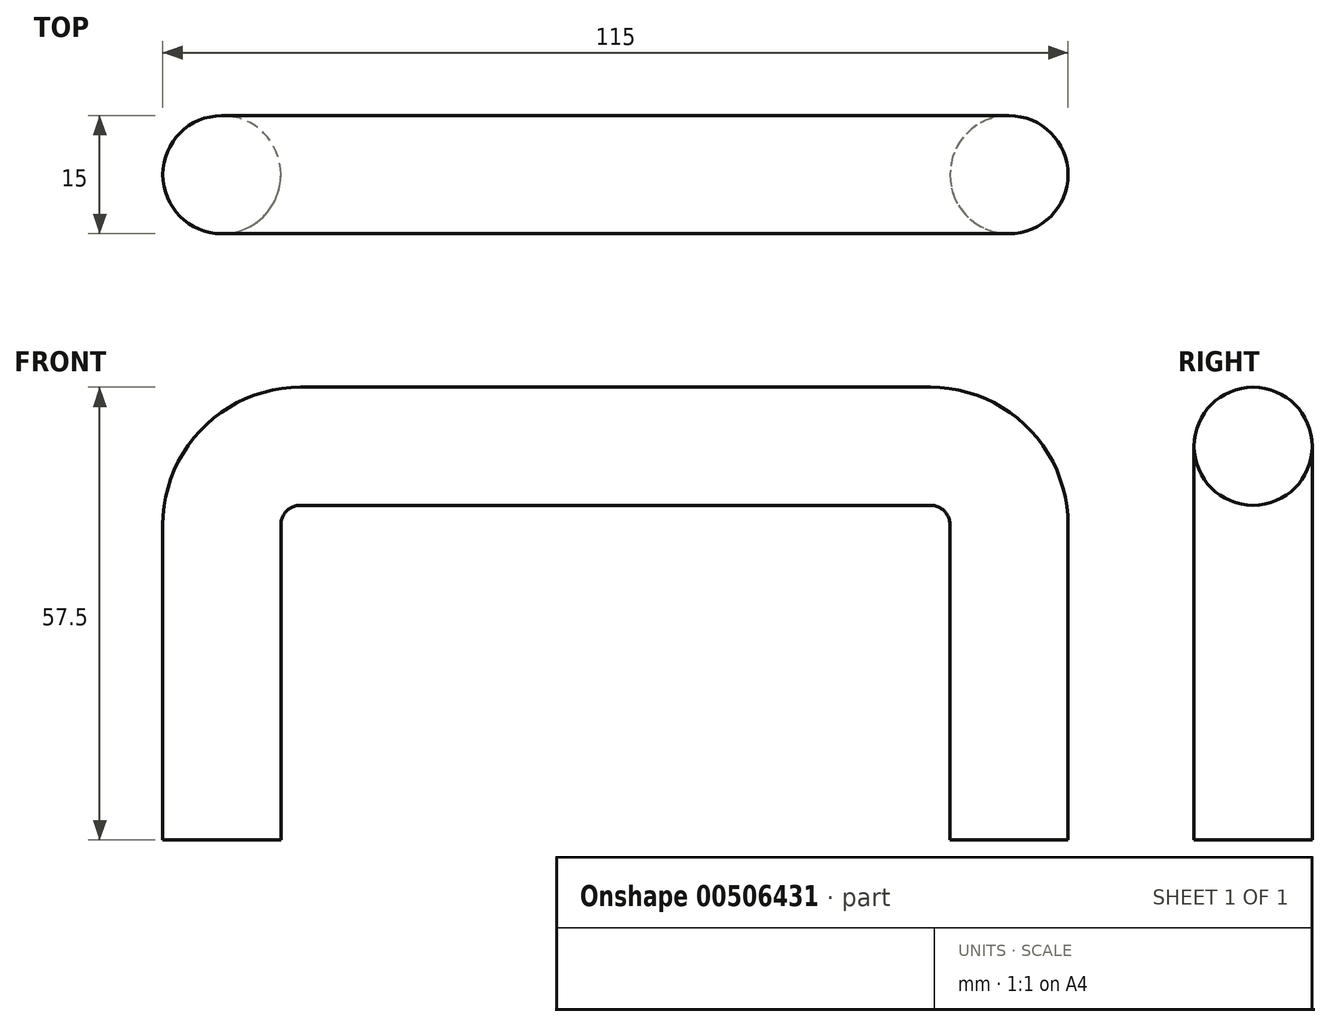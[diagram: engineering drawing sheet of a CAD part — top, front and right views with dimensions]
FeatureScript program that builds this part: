
annotation { "Feature Type Name" : "Feature", "Feature Type Description" : "" }
export const myFeature = defineFeature(function(context is Context, id is Id, definition is map)
    precondition{}
    {
        {
            var Q0;
            Q0=qCreatedBy(makeId("Top.planeOp"),FACE);
            cPlane(context, id + "F0", {"entities" : qUnion([Q0]), "cplaneType" : CPlaneType.OFFSET, "offset" : 25 * mm, "oppositeDirection" : true, "width" : 150 * mm, "height" : 150 * mm});
        }
        {
            var Q0;
            Q0=qCreatedBy(id+"F0.planeOp",FACE);
            var sketch = newSketch(context, id + "F1", { "sketchPlane" : qUnion([Q0])});
            skCircle(sketch, "E0", {"center": v(-50, 0) * mm, "radius": 7.5 * mm});
            skSolve(sketch);
        }
        {
            var Q0;
            Q0=qCreatedBy(makeId("Front.planeOp"),FACE);
            var sketch = newSketch(context, id + "F2", { "sketchPlane" : qUnion([Q0])});
            skLineSegment(sketch, "E1.top", {"start": v(-40, 25) * mm, "end": v(40, 25) * mm});
            skLineSegment(sketch, "E1.left", {"start": v(-50, -25) * mm, "end": v(-50, 15) * mm});
            skLineSegment(sketch, "E1.right", {"start": v(50, -25) * mm, "end": v(50, 15) * mm});
            skPoint(sketch, "E1.middle", {"position": v(0, 0) * mm});
            skPoint(sketch, "E2.visualSharp", {"position": v(50, 25) * mm});
            skArc(sketch, "E2.filletArc", {"start": v(50, 15) * mm, "mid": v(47.07, 22.07) * mm, "end": v(40, 25) * mm});
            skPoint(sketch, "E3.visualSharp", {"position": v(-50, 25) * mm});
            skArc(sketch, "E3.filletArc", {"start": v(-40, 25) * mm, "mid": v(-47.07, 22.07) * mm, "end": v(-50, 15) * mm});
            skSolve(sketch);
        }
        {
            var Q0;
            Q0=makeQuery(id+"F1.imprint","IMPRINT",FACE,{"disambiguationData":[TD([[makeQuery(id+"F1.imprint","IMPRINT",EDGE,{"derivedFrom":sQuery(id+"F1.wireOp",EDGE,"E0")}),1.0]])]});
            var Q1;
            Q1=sQuery(id+"F2.wireOp",EDGE,"E1.left");
            var Q2;
            Q2=sQuery(id+"F2.wireOp",EDGE,"E3.filletArc");
            var Q3;
            Q3=sQuery(id+"F2.wireOp",EDGE,"E1.top");
            var Q4;
            Q4=sQuery(id+"F2.wireOp",EDGE,"E2.filletArc");
            var Q5;
            Q5=sQuery(id+"F2.wireOp",EDGE,"E1.right");
            sweep(context, id + "F3", {"profiles" : qUnion([Q0]), "path" : qUnion([Q1, Q2, Q3, Q4, Q5])});
        }
    });
